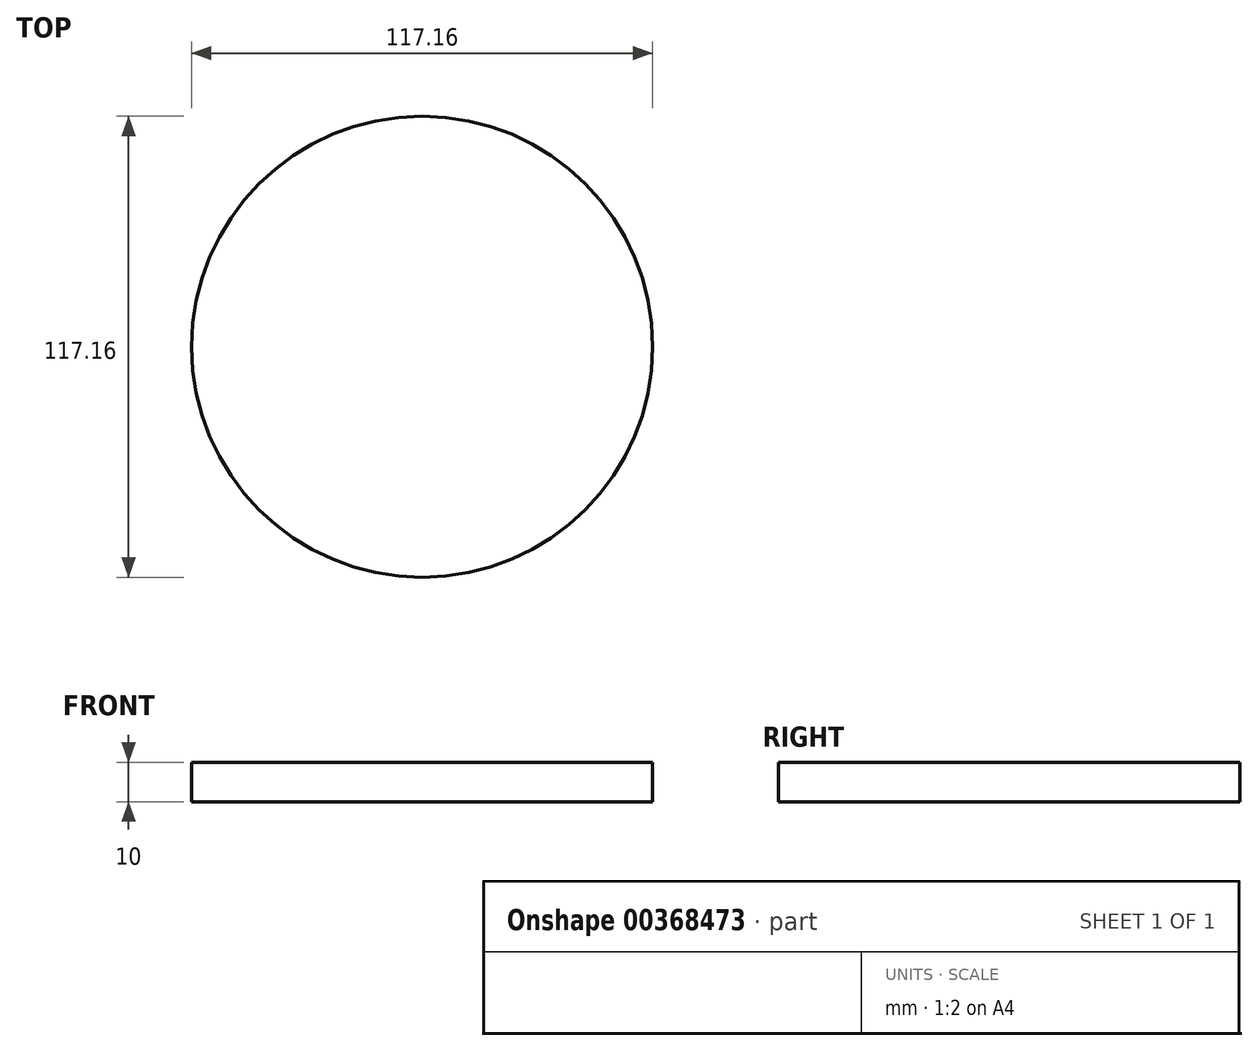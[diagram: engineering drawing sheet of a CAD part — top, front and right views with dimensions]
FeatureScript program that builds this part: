
annotation { "Feature Type Name" : "Feature", "Feature Type Description" : "" }
export const myFeature = defineFeature(function(context is Context, id is Id, definition is map)
    precondition{}
    {
        {
            var Q0;
            Q0=qCreatedBy(makeId("Top.planeOp"),FACE);
            var sketch = newSketch(context, id + "F0", { "sketchPlane" : qUnion([Q0])});
            skCircle(sketch, "E0", {"center": v(0, 0) * mm, "radius": 58.58 * mm});
            skSolve(sketch);
        }
        {
            var Q0;
            Q0 = qSketchRegion(id + "F0", true);
            extrude(context, id + "F1", {"entities" : qUnion([Q0]), "depth" : 10 * mm});
        }
    });
